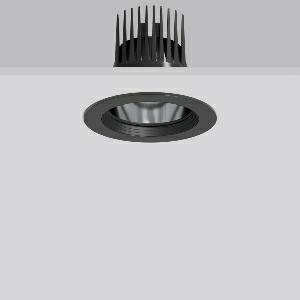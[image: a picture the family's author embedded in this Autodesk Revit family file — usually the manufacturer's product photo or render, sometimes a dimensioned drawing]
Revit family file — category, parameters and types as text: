
# Revit family: heledon_maxi_e_901758_003_2_c862
name_source: partatom
category: Lighting Fixtures
units: mm (PartAtom-declared; Revit-internal decimal feet)

## family parameters
Cut with Voids When Loaded = No
Host = Face
Light Source = No
Part Type = Normal
Room Calculation Point = No
Round Connector Dimension = Use Diameter
Shared = No

## types (1)
- HELEDON maxi E (1 x LED Modul 927, 3150 lm, 2700)
    Apparent Load = 25 VA
    Approval mark = CE
    CIE Flux Codes = 100 100 100 100 100
    Color Rendering = 92
    Color Temperature = 2700
    Default Elevation = 1800 mm
    Description = Series: HELEDON maxi
Round recessed downlight. Housing: die-cast aluminium, powder-coated. Black plastic ring and recessed LED to prevent glare from the side. Optical assembly with reflector made of MIRO-Silver with 98% total light reflection for outstanding efficiency - can be changed without tools. Best colour rendering index Ra>90. Suitable for Recessed ceiling mounting. Installation without tools thanks to spring fastening system. Including separate LED converter with connecting cable 600 mm.High quality converter without flickering and stroboscopic effect. Through-wiring box (5 pole) available as accessory. The following accessories can be mounted without use of tools: interchangeable lenses, decorative glasses, honeycomb louvre, clear and frosted diffusers, white interchangeable plastic ring. 
Colour: deep black, matt (RAL 9005)
Diameter: 162 mm
Height: 3 mm
Cut-out diameter: 152 mm
Recess height: 200 mm
Luminaire: recess height: 135 mm
Lamp: LED
Socket: without socket
Colour temperature: 2700K
Colour rendering index (CRI): 92
System power: 25 W
Rated luminous flux: 3150 lm
Luminous efficiency: 126 lm/W
Control gear: Regulated power supply
Protection class: II
Type of protection: IP 20
    Height = 0 mm  [stored 0 ft]
    Lamp = 1 x LED Modul 927
    Lamp Light Flux = 3150 lm
    Lamp count = 1
    Length = 162 mm
    Lifetime = 50000 h
    Luminous efficacy = 126 lm/W
    Manufacturer = RZB
    ModVariant = No
    Model = 901758.003.2
    Mounting Place = Ceiling
    Mounting Type = Recessed
    Number of Poles = 1
    OnlyDefault = Yes
    Power Factor = 1
    Product Name = HELEDON maxi E
    Product group = Recessed downlights
    ProductGroupID = 402
    Protection Class = Protection class II
    Protection Degree = IP 20
    RLX_Detail_Level = 1
    RLX_Emergency_Light_Flux = 0 lm
    RLX_Emergency_Type = 0
    RLX_Emergency_Type_DB = No
    RlxData = <blob elided: 122173 chars, md5=bd0587e6>
    Socket = socket
    Standby Power = 0 W
    System Light Flux = 3150 lm
    System Power = 25 W
    Type Comments = Product without accessories
    Type Image = 901662.003.jpg
    URL = http://relux.com
    VarID = ---
    Voltage = 230 V
    Voltage Range = 220-240 V
    Weight = 0.00 kg
    Width = 0 mm  [stored 0 ft]

note: [stored X ft] marks values corroborated as IEEE doubles in the binary element streams (Revit-internal decimal feet)

## geometry (parser evidence)
native form markers: Blend x4, Sweep x10
no freeform markers — native parametric forms only
